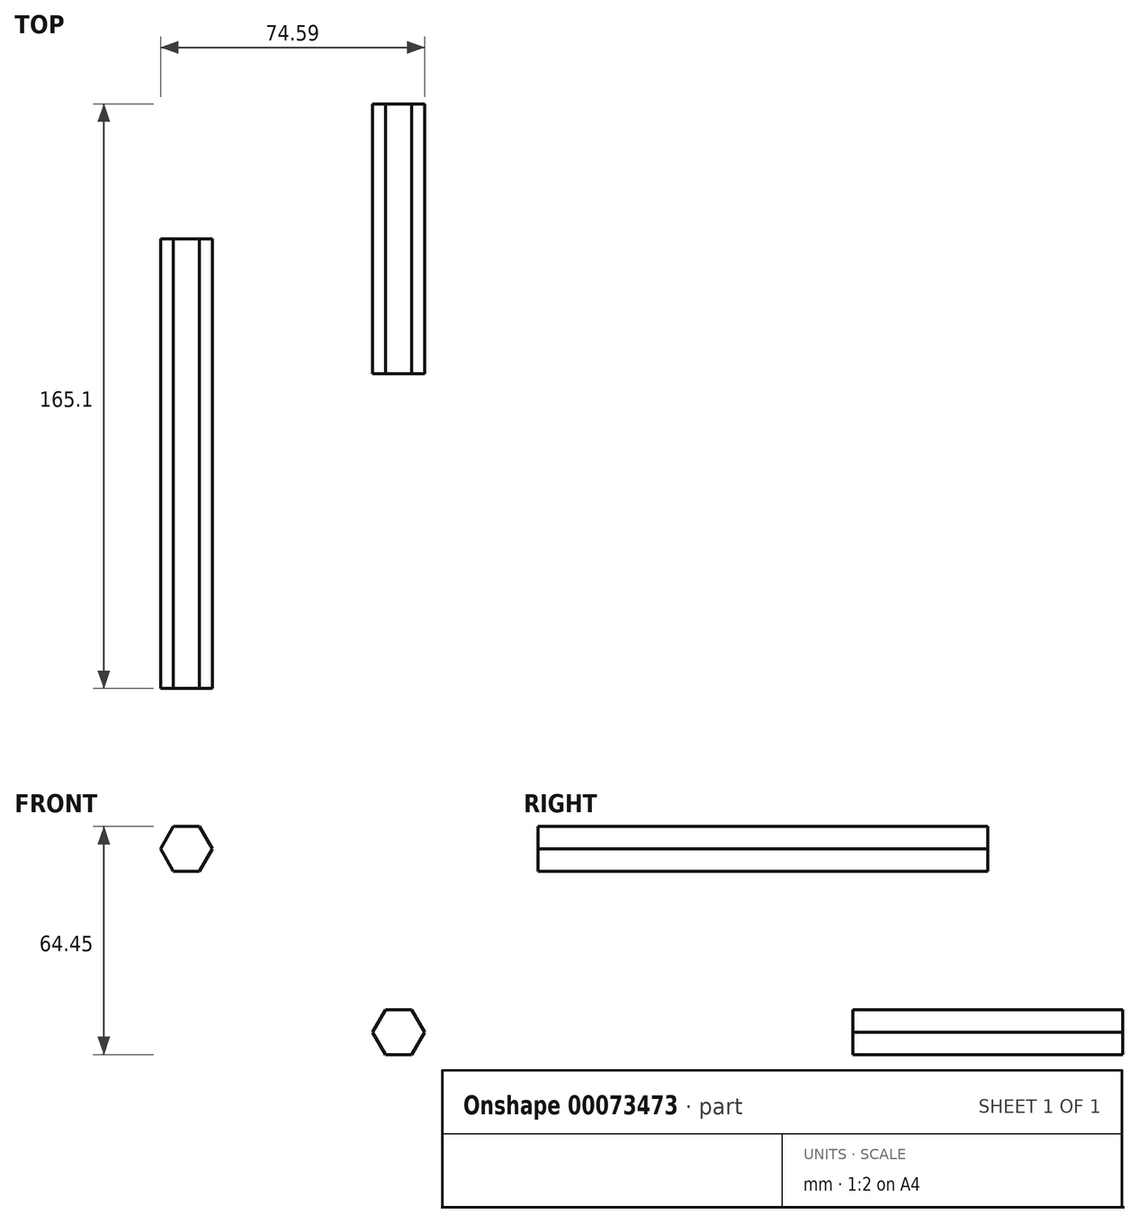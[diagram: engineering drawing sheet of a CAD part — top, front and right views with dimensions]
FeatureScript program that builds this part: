
annotation { "Feature Type Name" : "Feature", "Feature Type Description" : "" }
export const myFeature = defineFeature(function(context is Context, id is Id, definition is map)
    precondition{}
    {
        {
            var Q0;
            Q0=qCreatedBy(makeId("Front.planeOp"),FACE);
            var sketch = newSketch(context, id + "F0", { "sketchPlane" : qUnion([Q0])});
            skCircle(sketch, "E0.cCircle", {"center": v(0, 0) * mm, "radius": 6.35 * mm, "construction": true});
            skLineSegment(sketch, "E0.0", {"start": v(3.67, 6.35) * mm, "end": v(7.33, 0) * mm});
            skLineSegment(sketch, "E0.1", {"start": v(7.33, 0) * mm, "end": v(3.67, -6.35) * mm});
            skLineSegment(sketch, "E0.2", {"start": v(3.67, -6.35) * mm, "end": v(-3.67, -6.35) * mm});
            skLineSegment(sketch, "E0.3", {"start": v(-3.67, -6.35) * mm, "end": v(-7.33, 0) * mm});
            skLineSegment(sketch, "E0.4", {"start": v(-7.33, 0) * mm, "end": v(-3.67, 6.35) * mm});
            skLineSegment(sketch, "E0.5", {"start": v(-3.67, 6.35) * mm, "end": v(3.67, 6.35) * mm});
            skPoint(sketch, "E0.0.midPoint", {"position": v(5.5, 3.17) * mm});
            skSolve(sketch);
        }
        {
            var Q0;
            Q0=qSketchRegion(id+"F0",true);
            extrude(context, id + "F1", {"entities" : qUnion([Q0]), "endBound" : BoundingType.SYMMETRIC, "depth" : 76.2 * mm});
        }
        {
            var Q0;
            Q0=qCreatedBy(makeId("Front.planeOp"),FACE);
            var sketch = newSketch(context, id + "F2", { "sketchPlane" : qUnion([Q0])});
            skCircle(sketch, "E1.cCircle", {"center": v(-59.93, 51.75) * mm, "radius": 6.35 * mm, "construction": true});
            skLineSegment(sketch, "E1.0", {"start": v(-56.26, 58.1) * mm, "end": v(-52.6, 51.75) * mm});
            skLineSegment(sketch, "E1.1", {"start": v(-52.6, 51.75) * mm, "end": v(-56.26, 45.4) * mm});
            skLineSegment(sketch, "E1.2", {"start": v(-56.26, 45.4) * mm, "end": v(-63.6, 45.4) * mm});
            skLineSegment(sketch, "E1.3", {"start": v(-63.6, 45.4) * mm, "end": v(-67.26, 51.75) * mm});
            skLineSegment(sketch, "E1.4", {"start": v(-67.26, 51.75) * mm, "end": v(-63.6, 58.1) * mm});
            skLineSegment(sketch, "E1.5", {"start": v(-63.6, 58.1) * mm, "end": v(-56.26, 58.1) * mm});
            skPoint(sketch, "E1.0.midPoint", {"position": v(-54.43, 54.93) * mm});
            skSolve(sketch);
        }
        {
            var Q0;
            Q0=makeQuery(id+"F2.imprint","IMPRINT",FACE,{"disambiguationData":[TD([[makeQuery(id+"F2.imprint","IMPRINT",EDGE,{"derivedFrom":sQuery(id+"F2.wireOp",EDGE,"E1.0")}),-1.0]])]});
            extrude(context, id + "F3", {"entities" : qUnion([Q0]), "depth" : 127 * mm});
        }
    });
